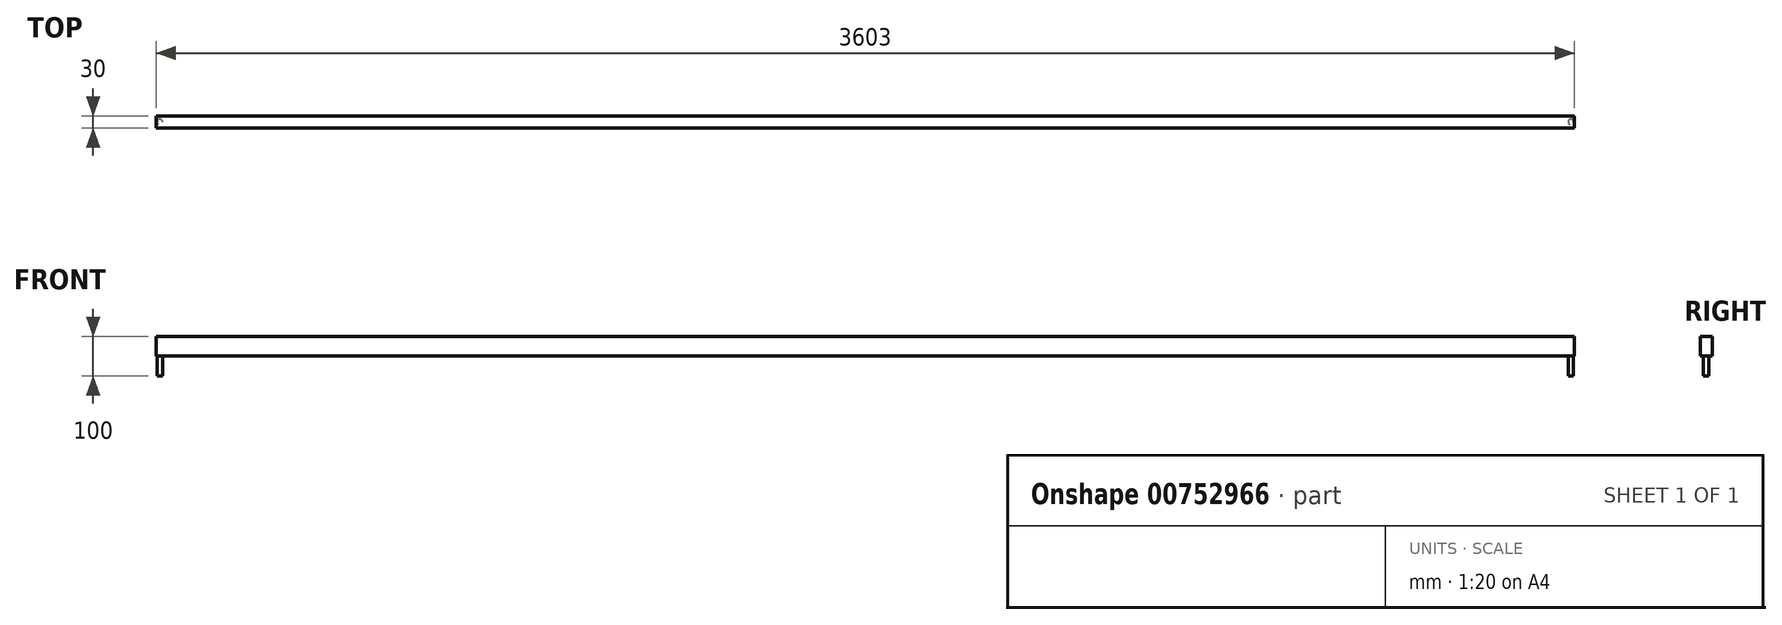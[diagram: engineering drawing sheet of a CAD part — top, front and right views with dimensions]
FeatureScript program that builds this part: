
annotation { "Feature Type Name" : "Feature", "Feature Type Description" : "" }
export const myFeature = defineFeature(function(context is Context, id is Id, definition is map)
    precondition{}
    {
        {
            var Q0;
            Q0=qCreatedBy(makeId("Front.planeOp"),FACE);
            var sketch = newSketch(context, id + "F0", { "sketchPlane" : qUnion([Q0])});
            skLineSegment(sketch, "E0.bottom", {"start": v(1801.5, -25) * mm, "end": v(-1801.5, -25) * mm});
            skLineSegment(sketch, "E0.top", {"start": v(1801.5, 25) * mm, "end": v(-1801.5, 25) * mm});
            skLineSegment(sketch, "E0.left", {"start": v(1801.5, -25) * mm, "end": v(1801.5, 25) * mm});
            skLineSegment(sketch, "E0.right", {"start": v(-1801.5, -25) * mm, "end": v(-1801.5, 25) * mm});
            skPoint(sketch, "E0.middle", {"position": v(0, 0) * mm});
            skSolve(sketch);
        }
        {
            var Q0;
            Q0 = qSketchRegion(id + "F0", true);
            extrude(context, id + "F1", {"entities" : qUnion([Q0]), "depth" : 15 * mm, "offsetDistance" : 25 * mm, "hasSecondDirection" : true, "secondDirectionOppositeDirection" : true, "secondDirectionDepth" : 15 * mm});
        }
        {
            var Q0;
            Q0=makeQuery(id+"F1.opExtrude","SWEPT_FACE",FACE,{"disambiguationData":[OSD([sQuery(id+"F0.wireOp",EDGE,"E0.bottom")])]});
            var sketch = newSketch(context, id + "F2", { "sketchPlane" : qUnion([Q0])});
            skLineSegment(sketch, "E1.0", {"start": v(-1801.5, 15) * mm, "end": v(-1801.5, -15) * mm});
            skLineSegment(sketch, "E2", {"start": v(-1801.5, 0) * mm, "end": v(-1799.5, 0) * mm});
            skLineSegment(sketch, "E3", {"start": v(-1799.5, 0) * mm, "end": v(-1792.5, 0) * mm});
            skCircle(sketch, "E4", {"center": v(-1792.5, 0) * mm, "radius": 7 * mm});
            skSolve(sketch);
        }
        {
            var Q0;
            Q0 = qSketchRegion(id + "F2", true);
            extrude(context, id + "F3", {"entities" : qUnion([Q0]), "operationType" : NewBodyOperationType.ADD, "depth" : 50 * mm, "offsetDistance" : 25 * mm});
        }
        {
            var Q0;
            Q0=makeQuery(id+"F1.opExtrude","SWEPT_FACE",FACE,{"disambiguationData":[OSD([sQuery(id+"F0.wireOp",EDGE,"E0.bottom")])]});
            var sketch = newSketch(context, id + "F4", { "sketchPlane" : qUnion([Q0])});
            skLineSegment(sketch, "E5.0", {"start": v(1801.5, 15) * mm, "end": v(1801.5, -15) * mm});
            skLineSegment(sketch, "E6", {"start": v(1801.5, 0) * mm, "end": v(1799.5, 0) * mm});
            skLineSegment(sketch, "E7", {"start": v(1799.5, 0) * mm, "end": v(1792.5, 0) * mm});
            skCircle(sketch, "E8", {"center": v(1792.5, 0) * mm, "radius": 7 * mm});
            skSolve(sketch);
        }
        {
            var Q0;
            Q0 = qSketchRegion(id + "F4", true);
            extrude(context, id + "F5", {"entities" : qUnion([Q0]), "operationType" : NewBodyOperationType.ADD, "depth" : 50 * mm, "offsetDistance" : 25 * mm});
        }
    });
